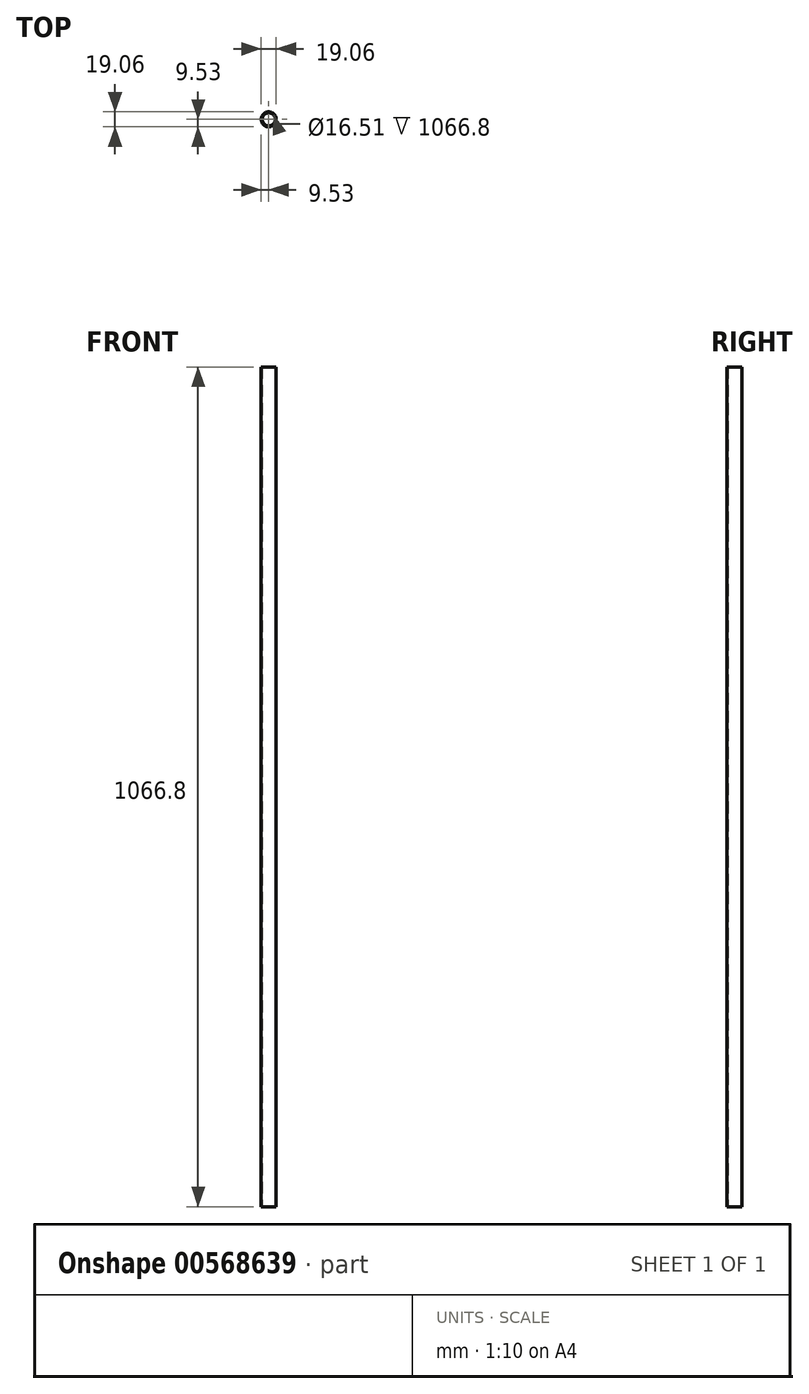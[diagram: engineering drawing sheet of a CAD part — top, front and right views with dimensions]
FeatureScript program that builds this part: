
annotation { "Feature Type Name" : "Feature", "Feature Type Description" : "" }
export const myFeature = defineFeature(function(context is Context, id is Id, definition is map)
    precondition{}
    {
        {
            var Q0;
            Q0=qCreatedBy(makeId("Top.planeOp"),FACE);
            var sketch = newSketch(context, id + "F0", { "sketchPlane" : qUnion([Q0])});
            skCircle(sketch, "E0", {"center": v(0, 0) * mm, "radius": 9.52 * mm});
            skCircle(sketch, "E1", {"center": v(0, 0) * mm, "radius": 8.26 * mm});
            skSolve(sketch);
        }
        {
            var Q0;
            Q0 = qSketchRegion(id + "F0", true);
            extrude(context, id + "F1", {"entities" : qUnion([Q0]), "depth" : 1066.8 * mm, "offsetDistance" : 25.4 * mm});
        }
    });
